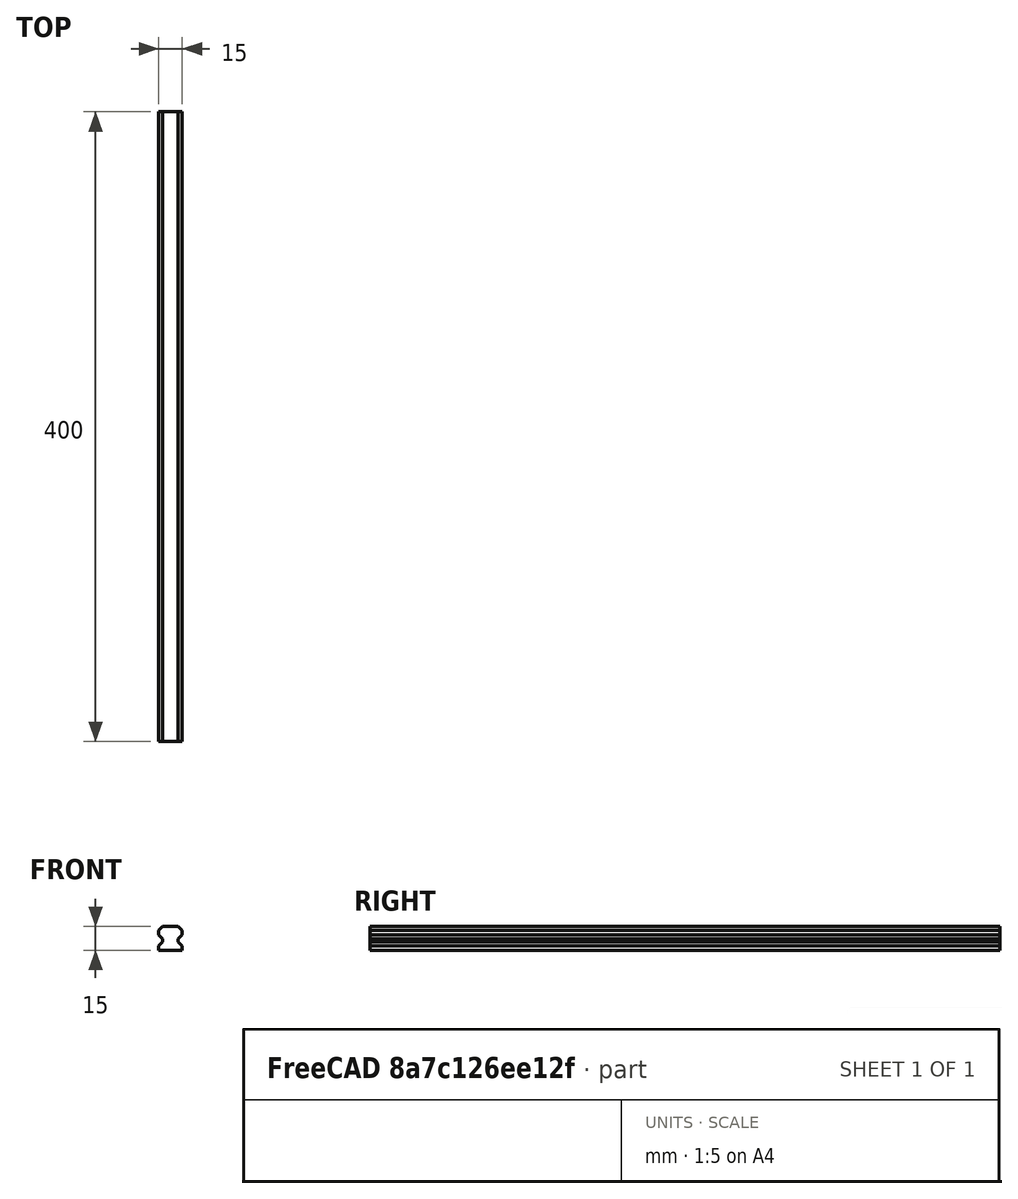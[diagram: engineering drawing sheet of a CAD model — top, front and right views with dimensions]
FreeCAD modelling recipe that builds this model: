
FCSTD DOCUMENT  (FreeCAD 0.19R)
Label: x_rail
License: All rights reserved
LicenseURL: http://en.wikipedia.org/wiki/All_rights_reserved
objects: PartDesign::CoordinateSystem×2, Sketcher::SketchObject×1, PartDesign::Pad×1, PartDesign::Body×1
note: 6 computed .brp shape members not serialized (recipe doc carries the construction recipe); baked Part::Feature solids carry a one-line shape summary decoded from their .brp

FEATURE [Sketcher::SketchObject] Sketch
  FullyConstrained = true
  MapMode = 5
  Placement = pos=(0,0,0) rot=(1,0,0;1.5708rad)
  Support = -> [XZ_Plane]
  sketch-geometry (14):
    g0: LineSegment StartX=-7.5 StartY=0 StartZ=0 EndX=7.5 EndY=0 EndZ=0
    g1: LineSegment StartX=-7.5 StartY=0 StartZ=0 EndX=-7.5 EndY=2.7 EndZ=0
    g2: LineSegment StartX=7.5 StartY=0 StartZ=0 EndX=7.5 EndY=2.7 EndZ=0
    g3: LineSegment StartX=-7.5 StartY=2.7 StartZ=0 EndX=-5 EndY=5.2 EndZ=0
    g4: LineSegment StartX=-5 StartY=5.2 StartZ=0 EndX=-5 EndY=7.2 EndZ=0
    g5: LineSegment StartX=-5 StartY=7.2 StartZ=0 EndX=-7.5 EndY=9.7 EndZ=0
    g6: LineSegment StartX=-7.5 StartY=9.7 StartZ=0 EndX=-7.5 EndY=12.5 EndZ=0
    g7: LineSegment StartX=-7.5 StartY=12.5 StartZ=0 EndX=-5 EndY=15 EndZ=0
    g8: LineSegment StartX=-5 StartY=15 StartZ=0 EndX=5 EndY=15 EndZ=0
    g9: LineSegment StartX=5 StartY=15 StartZ=0 EndX=7.5 EndY=12.5 EndZ=0
    g10: LineSegment StartX=7.5 StartY=12.5 StartZ=0 EndX=7.5 EndY=9.7 EndZ=0
    g11: LineSegment StartX=7.5 StartY=9.7 StartZ=0 EndX=5 EndY=7.2 EndZ=0
    g12: LineSegment StartX=5 StartY=7.2 StartZ=0 EndX=5 EndY=5.2 EndZ=0
    g13: LineSegment StartX=7.5 StartY=2.7 StartZ=0 EndX=5 EndY=5.2 EndZ=0
  constraints (36):
    c: PointOnObject(g0,g-1)
    c: Coincident(g1,g0)
    c: Vertical(g1)
    c: Coincident(g2,g0)
    c: Vertical(g2)
    c: Coincident(g3,g1)
    c: Coincident(g4,g3)
    c: Vertical(g4)
    c: Coincident(g5,g4)
    c: Coincident(g6,g5)
    c: Coincident(g7,g6)
    c: Coincident(g8,g7)
    c: Coincident(g9,g8)
    c: Coincident(g10,g9)
    c: Coincident(g11,g10)
    c: Coincident(g12,g11)
    c: Coincident(g13,g2)
    c: Coincident(g13,g12)
    c: Symmetric(g0,g0,g-2)
    c: DistanceX(g0,g0) = 15
    c: DistanceY(g0,g8) = 15
    c: DistanceX(g8,g8) = 10
    c: Symmetric(g7,g8,g-2)
    c: Vertical(g6)
    c: Symmetric(g9,g6,g-2)
    c: Symmetric(g5,g10,g-2)
    c: Symmetric(g4,g11,g-2)
    c: Symmetric(g12,g3,g-2)
    c: DistanceX(g8,g9) = 2.5
    c: DistanceY(g9,g8) = 2.5
    c: DistanceY(g11,g10) = 2.5
    c: DistanceY(g13,g13) = 2.5
    c: DistanceY(g12,g12) = 2
    c: DistanceY(g10,g10) = 2.8
    c: DistanceX(g11,g11) = 2.5
    c: Equal(g2,g1)
FEATURE [PartDesign::Pad] Pad
  Direction = (1,1,1)
  Length = 400
  Length2 = 100
  Placement = pos=(0,0,0) rot=(1,0,0;1.5708rad)
  Profile = -> Sketch
  Type = 0
FEATURE [PartDesign::CoordinateSystem] LCS_mount
  AttacherType = Attacher::AttachEngine3D
  AttachmentOffset = pos=(0,30,0) rot=(0,0,1;0rad)
  MapMode = 5
  Placement = pos=(0,-30,1.32e-14) rot=(1,0,0;3.14159rad)
  Support = -> [Pad]
FEATURE [PartDesign::CoordinateSystem] LCS_CARET_MOUNT
  AttacherType = Attacher::AttachEngine3D
  AttachmentOffset = pos=(0,100,0) rot=(0,0,1;0rad)
  MapMode = 5
  Placement = pos=(0,-100,15) rot=(0,0,1;3.14159rad)
  Support = -> [Pad]
FEATURE [PartDesign::Body] Body
  Group = -> [Sketch,Pad,LCS_mount,LCS_CARET_MOUNT]
  Origin = -> Origin
  Tip = -> Pad
